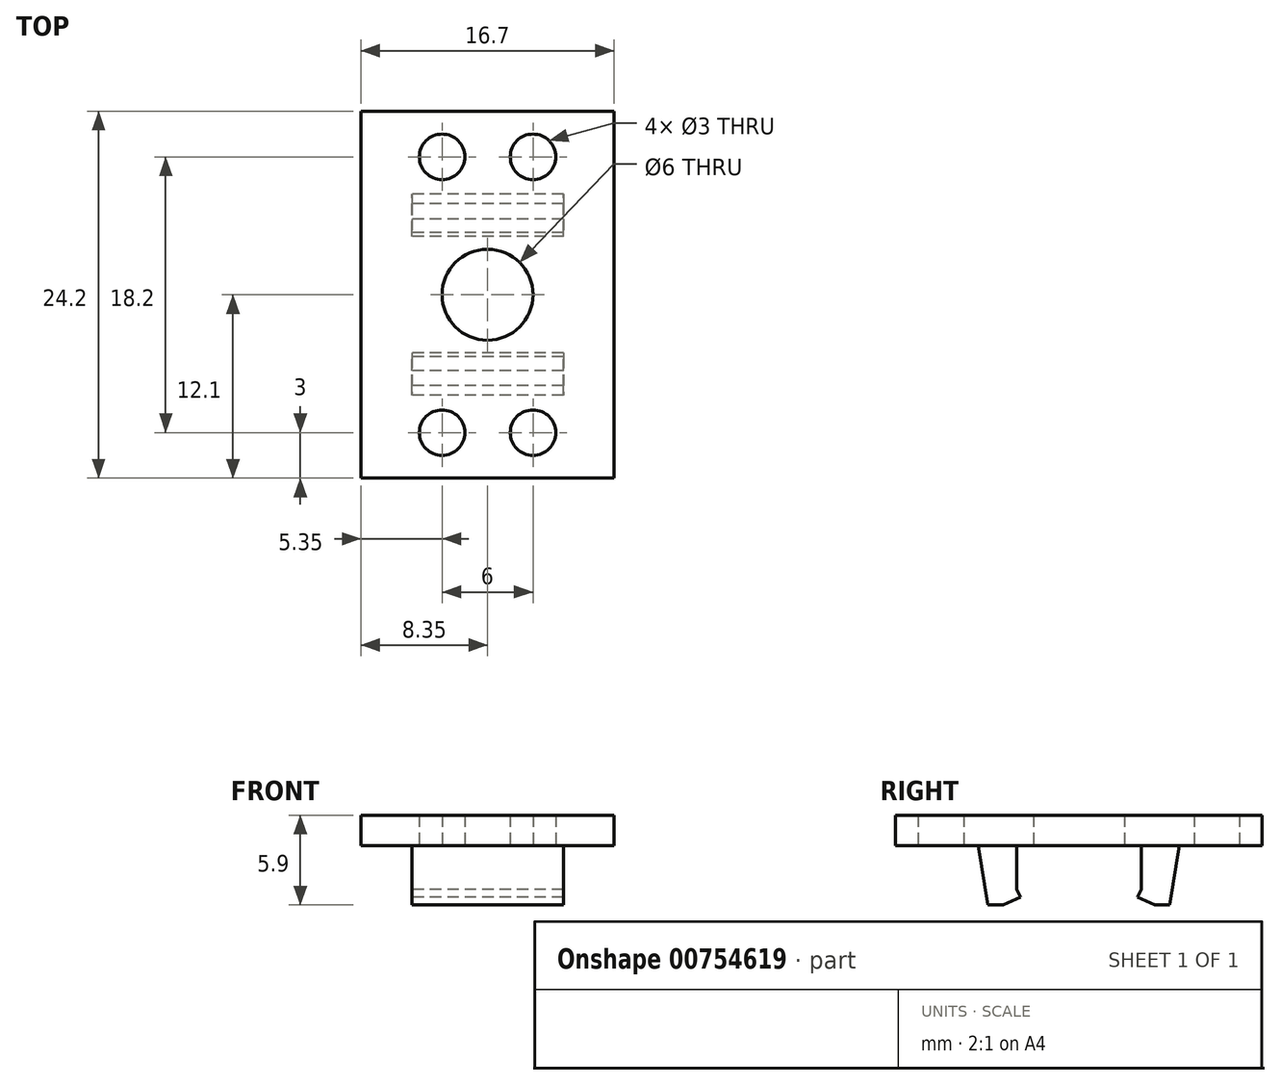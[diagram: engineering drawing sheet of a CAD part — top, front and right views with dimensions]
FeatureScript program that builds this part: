
annotation { "Feature Type Name" : "Feature", "Feature Type Description" : "" }
export const myFeature = defineFeature(function(context is Context, id is Id, definition is map)
    precondition{}
    {
        {
            var Q0;
            Q0=qCreatedBy(makeId("Top.planeOp"),FACE);
            var sketch = newSketch(context, id + "F0", { "sketchPlane" : qUnion([Q0])});
            skLineSegment(sketch, "E0.bottom", {"start": v(4.35, 4.1) * mm, "end": v(-4.35, 4.1) * mm, "construction": true});
            skLineSegment(sketch, "E0.top", {"start": v(4.35, -4.1) * mm, "end": v(-4.35, -4.1) * mm, "construction": true});
            skLineSegment(sketch, "E0.left", {"start": v(4.35, 4.1) * mm, "end": v(4.35, -4.1) * mm, "construction": true});
            skLineSegment(sketch, "E0.right", {"start": v(-4.35, 4.1) * mm, "end": v(-4.35, -4.1) * mm, "construction": true});
            skPoint(sketch, "E0.middle", {"position": v(0, 0) * mm});
            skLineSegment(sketch, "E1.bottom", {"start": v(8.35, 12.1) * mm, "end": v(-8.35, 12.1) * mm});
            skLineSegment(sketch, "E1.top", {"start": v(8.35, -12.1) * mm, "end": v(-8.35, -12.1) * mm});
            skLineSegment(sketch, "E1.left", {"start": v(8.35, 12.1) * mm, "end": v(8.35, -12.1) * mm});
            skLineSegment(sketch, "E1.right", {"start": v(-8.35, 12.1) * mm, "end": v(-8.35, -12.1) * mm});
            skCircle(sketch, "E2", {"center": v(-3, -9.1) * mm, "radius": 1.5 * mm});
            skLineSegment(sketch, "E3", {"start": v(0, -12.1) * mm, "end": v(0, 0) * mm, "construction": true});
            skCircle(sketch, "E4.MirrorC", {"center": v(3, -9.1) * mm, "radius": 1.5 * mm});
            skCircle(sketch, "E5", {"center": v(0, 0) * mm, "radius": 3 * mm});
            skLineSegment(sketch, "E6", {"start": v(0, 0) * mm, "end": v(-8.35, 0) * mm, "construction": true});
            skCircle(sketch, "E7.MirrorC", {"center": v(3, 9.1) * mm, "radius": 1.5 * mm});
            skCircle(sketch, "E8.MirrorC", {"center": v(-3, 9.1) * mm, "radius": 1.5 * mm});
            skSolve(sketch);
        }
        {
            var Q0;
            Q0 = qSketchRegion(id + "F0", true);
            extrude(context, id + "F1", {"entities" : qUnion([Q0]), "depth" : 2 * mm, "offsetDistance" : 25.4 * mm});
        }
        {
            var Q0;
            Q0=qCreatedBy(makeId("Top.planeOp"),FACE);
            var sketch = newSketch(context, id + "F2", { "sketchPlane" : qUnion([Q0])});
            skLineSegment(sketch, "E9", {"start": v(5, -6.35) * mm, "end": v(-5, -6.35) * mm});
            skLineSegment(sketch, "E10", {"start": v(-5, 0) * mm, "end": v(0, 0) * mm, "construction": true});
            skLineSegment(sketch, "E11", {"start": v(0, -6.35) * mm, "end": v(0, 0) * mm, "construction": true});
            skLineSegment(sketch, "E12", {"start": v(-5, -6.35) * mm, "end": v(-5, -4.35) * mm});
            skLineSegment(sketch, "E13", {"start": v(-5, -4.35) * mm, "end": v(5, -4.35) * mm});
            skLineSegment(sketch, "E14", {"start": v(5, -4.35) * mm, "end": v(5, -6.35) * mm});
            skLineSegment(sketch, "E15.MirrorCS", {"start": v(5, 4.35) * mm, "end": v(5, 6.35) * mm});
            skLineSegment(sketch, "E16.MirrorCS", {"start": v(-5, 4.35) * mm, "end": v(5, 4.35) * mm});
            skLineSegment(sketch, "E17.MirrorCS", {"start": v(5, 6.35) * mm, "end": v(-5, 6.35) * mm});
            skLineSegment(sketch, "E18.MirrorCS", {"start": v(-5, 6.35) * mm, "end": v(-5, 4.35) * mm});
            skSolve(sketch);
        }
        {
            var Q0;
            Q0=qCreatedBy(makeId("Right.planeOp"),FACE);
            var sketch = newSketch(context, id + "F3", { "sketchPlane" : qUnion([Q0])});
            skLineSegment(sketch, "E19", {"start": v(-6.64, 0) * mm, "end": v(-6, -3.9) * mm});
            skLineSegment(sketch, "E20", {"start": v(-6, -3.9) * mm, "end": v(-5, -3.9) * mm});
            skLineSegment(sketch, "E21", {"start": v(-5, -3.9) * mm, "end": v(-3.85, -3.4) * mm});
            skLineSegment(sketch, "E22", {"start": v(-3.85, -3.4) * mm, "end": v(-4.1, -2.9) * mm});
            skLineSegment(sketch, "E23", {"start": v(-4.1, -2.9) * mm, "end": v(-4.1, 0) * mm});
            skLineSegment(sketch, "E24", {"start": v(-4.1, 0) * mm, "end": v(-6.64, 0) * mm});
            skLineSegment(sketch, "E25", {"start": v(0, 0) * mm, "end": v(0, -3.9) * mm, "construction": true});
            skLineSegment(sketch, "E26", {"start": v(0, -3.9) * mm, "end": v(-5, -3.9) * mm, "construction": true});
            skLineSegment(sketch, "E27.MirrorCS", {"start": v(4.1, 0) * mm, "end": v(6.64, 0) * mm});
            skLineSegment(sketch, "E28.MirrorCS", {"start": v(5, -3.9) * mm, "end": v(3.85, -3.4) * mm});
            skLineSegment(sketch, "E29.MirrorCS", {"start": v(3.85, -3.4) * mm, "end": v(4.1, -2.9) * mm});
            skLineSegment(sketch, "E30.MirrorCS", {"start": v(4.1, -2.9) * mm, "end": v(4.1, 0) * mm});
            skLineSegment(sketch, "E31.MirrorCS", {"start": v(6, -3.9) * mm, "end": v(5, -3.9) * mm});
            skLineSegment(sketch, "E32.MirrorCS", {"start": v(6.64, 0) * mm, "end": v(6, -3.9) * mm});
            skSolve(sketch);
        }
        {
            var Q0;
            Q0 = qSketchRegion(id + "F3", true);
            extrude(context, id + "F4", {"entities" : qUnion([Q0]), "operationType" : NewBodyOperationType.ADD, "endBound" : BoundingType.SYMMETRIC, "depth" : 10 * mm, "offsetDistance" : 25.4 * mm});
        }
    });
